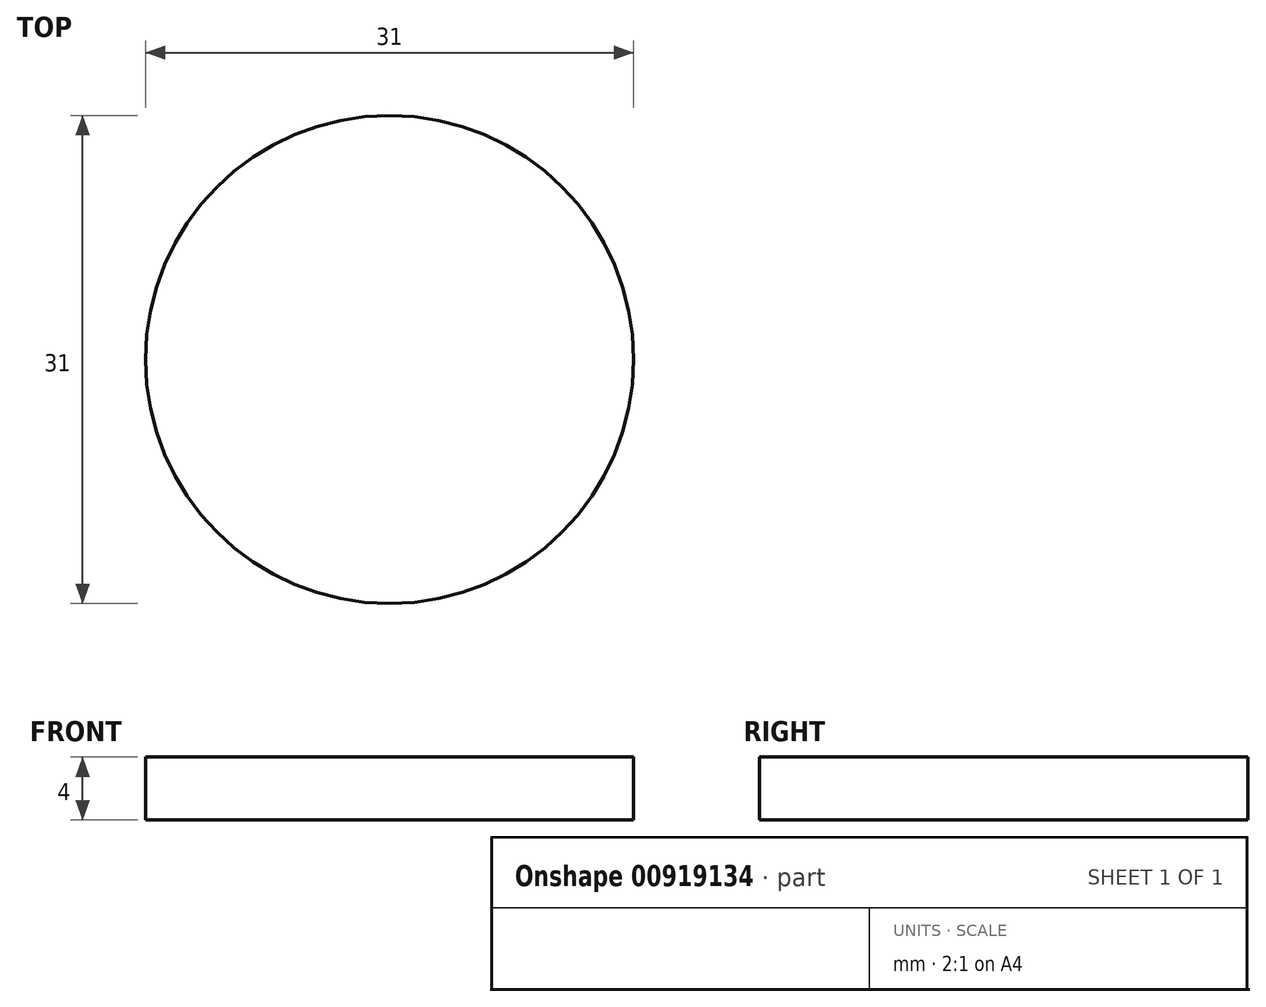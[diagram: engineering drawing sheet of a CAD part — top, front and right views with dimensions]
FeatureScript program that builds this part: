
annotation { "Feature Type Name" : "Feature", "Feature Type Description" : "" }
export const myFeature = defineFeature(function(context is Context, id is Id, definition is map)
    precondition{}
    {
        {
            var Q0;
            Q0=qCreatedBy(makeId("Top.planeOp"),FACE);
            var sketch = newSketch(context, id + "F0", { "sketchPlane" : qUnion([Q0])});
            skCircle(sketch, "E0", {"center": v(0, 0) * mm, "radius": 15.5 * mm});
            skSolve(sketch);
        }
        {
            var Q0;
            Q0=makeQuery(id+"F0.imprint","IMPRINT",FACE,{"disambiguationData":[TD([[makeQuery(id+"F0.imprint","IMPRINT",EDGE,{"derivedFrom":sQuery(id+"F0.wireOp",EDGE,"E0")}),1.0]])]});
            extrude(context, id + "F1", {"entities" : qUnion([Q0]), "depth" : 4 * mm, "offsetDistance" : 25 * mm});
        }
    });
